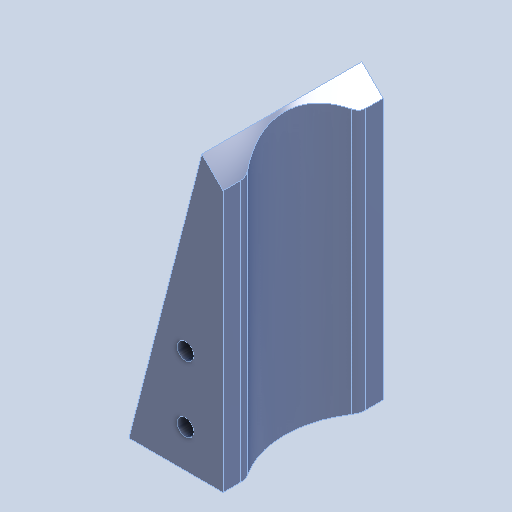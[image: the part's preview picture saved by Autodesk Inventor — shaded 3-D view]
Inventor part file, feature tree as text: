
AUTODESK INVENTOR PART (.ipt)
format: ipt  version: 2024.2 (Build 282272000, 272)  size: 292,864 bytes
history: native  units: mm
features: extrude x5, sketch x5, chamfer x1, shell x1, fillet x1, plane x1, mirror x1
ambient origin geometry x8: Origin, YZ Plane, XZ Plane, XY Plane, X Axis, Y Axis, Z Axis, Center Point
bodies: Solid1 (feature_tree)
feature tree (15):
  extrude  "Extrusion1"  Depth=20.0mm
  chamfer  "Chamfer1"  Distance=60.0mm
  extrude  "Extrusion2"  Depth=60.0mm TaperAngle=0.0deg
  extrude  "Extrusion7"  Depth=16.0mm
  shell  "Shell2"  Thickness=0.0mm
  extrude  "Extrusion8"  Depth=3.0mm
  fillet  "Fillet2"  Radius=4.5mm
  extrude  "Extrusion9"  Depth=10.0mm
  plane  "Work Plane1"
  mirror  "Mirror1"
  sketch  "Sketch1"  dims[d0=34.0mm d1=20.0mm d2=60.0mm d3=0.0mm]
  sketch  "Sketch3"  dims[d4=4.5mm d5=2.0mm d6=45.0deg d7=60.0mm d8=0.0mm]
  sketch  "Sketch8"  dims[d44=40.0mm d45=16.0mm d46=0.0mm d47=0.0mm]
  sketch  "Sketch9"  dims[d48=3.0mm d49=4.5mm d50=4.5mm]
  sketch  "Sketch10"  dims[d51=5.0mm d52=10.0mm d53=360.0deg d54=4.5mm d56=25.0mm d57=3.0mm d58=0.0mm d59=4.0mm d60=3.5mm d61=12.0mm d62=8.0mm d64=3.5mm d65=3.0mm d66=0.0mm d67=-17.0mm d17=0.5mm d18=0.872665mm d19=0.5mm d20=0.872665mm]
